# Revit family: 1 SOUND_C-Clamp_Cannon Series
name_source: partatom
category: Communication Devices
units: mm (PartAtom-declared; Revit-internal decimal feet)

## family parameters
Cut with Voids When Loaded = No
Host = Face
Maintain Annotation Orientation = No
Part Type = Normal
Room Calculation Point = No
Round Connector Dimension = Use Diameter
Shared = No

## types (3) — shared parameters
Category = Accessory
Construction = Galvanized Steel or Stainless Steel 316
Default Elevation = 2438.40 mm
Finish = Powder Coated or Brushed Stainless Steel
Manufacturer = 1 SOUND
Material = Zinc Plated
URL = https://www.1-sound.com

## per-type parameters (varying)
| type | Depth - Overall | Dimensions (HxWxD) | Model | Weight | Width - Mounting Holes | Width - Overall |
| C6 C-Clamp | 172.70 mm | 25.40mm x 225.00mm x 172.70mm | C-Clamp; C6 | .28 kg | 70.00 mm | 225.00 mm |
| C5 C-Clamp | 167.00 mm | 25.40mm x 200.00mm x 167.00mm | C-Clamp; C5 | .26 kg | 70.00 mm | 200.00 mm |
| C4i C-Clamp | 145.00 mm | 25.40mm x 160.00mm x 145.00mm | C-Clamp; C4i | .22 kg | 52.50 mm | 160.00 mm |

## geometry (parser evidence)
native form markers: Sweep x2
no freeform markers — native parametric forms only
